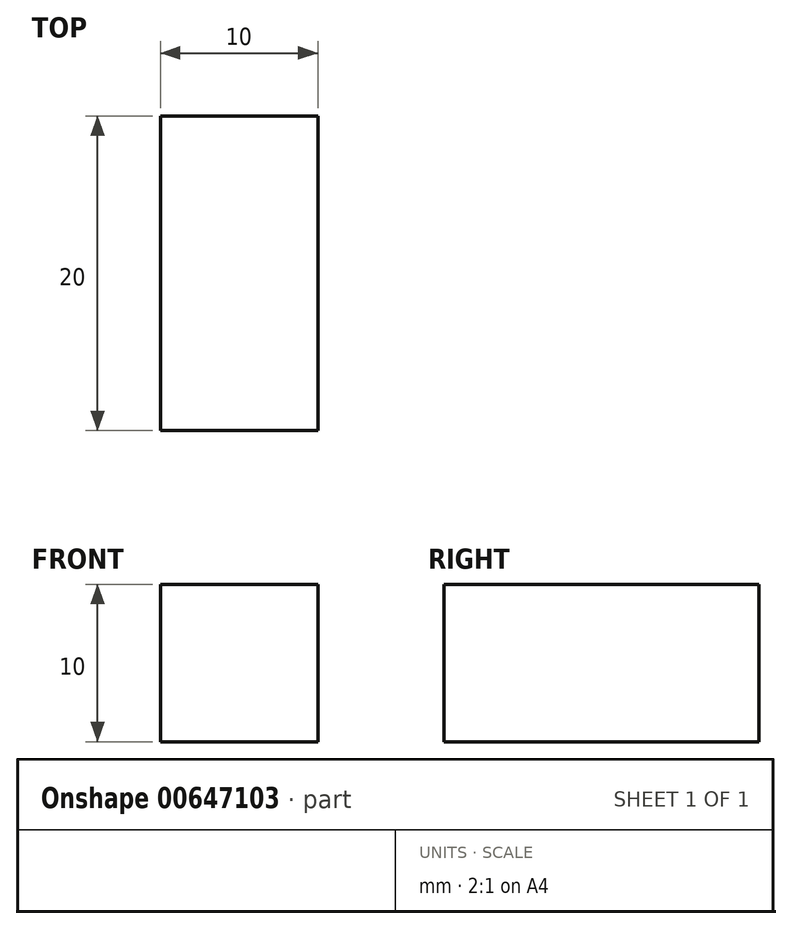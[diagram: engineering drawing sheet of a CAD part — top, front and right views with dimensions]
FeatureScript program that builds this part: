
annotation { "Feature Type Name" : "Feature", "Feature Type Description" : "" }
export const myFeature = defineFeature(function(context is Context, id is Id, definition is map)
    precondition{}
    {
        {
            var Q0;
            Q0=qCreatedBy(makeId("Top.planeOp"),FACE);
            var sketch = newSketch(context, id + "F0", { "sketchPlane" : qUnion([Q0])});
            skLineSegment(sketch, "E0.bottom", {"start": v(0, 0) * mm, "end": v(10, 0) * mm});
            skLineSegment(sketch, "E0.top", {"start": v(0, 20) * mm, "end": v(10, 20) * mm});
            skLineSegment(sketch, "E0.left", {"start": v(0, 0) * mm, "end": v(0, 20) * mm});
            skLineSegment(sketch, "E0.right", {"start": v(10, 0) * mm, "end": v(10, 20) * mm});
            skSolve(sketch);
        }
        {
            var Q0;
            Q0 = qSketchRegion(id + "F0", true);
            extrude(context, id + "F1", {"entities" : qUnion([Q0]), "depth" : 10 * mm, "offsetDistance" : 25 * mm});
        }
    });
